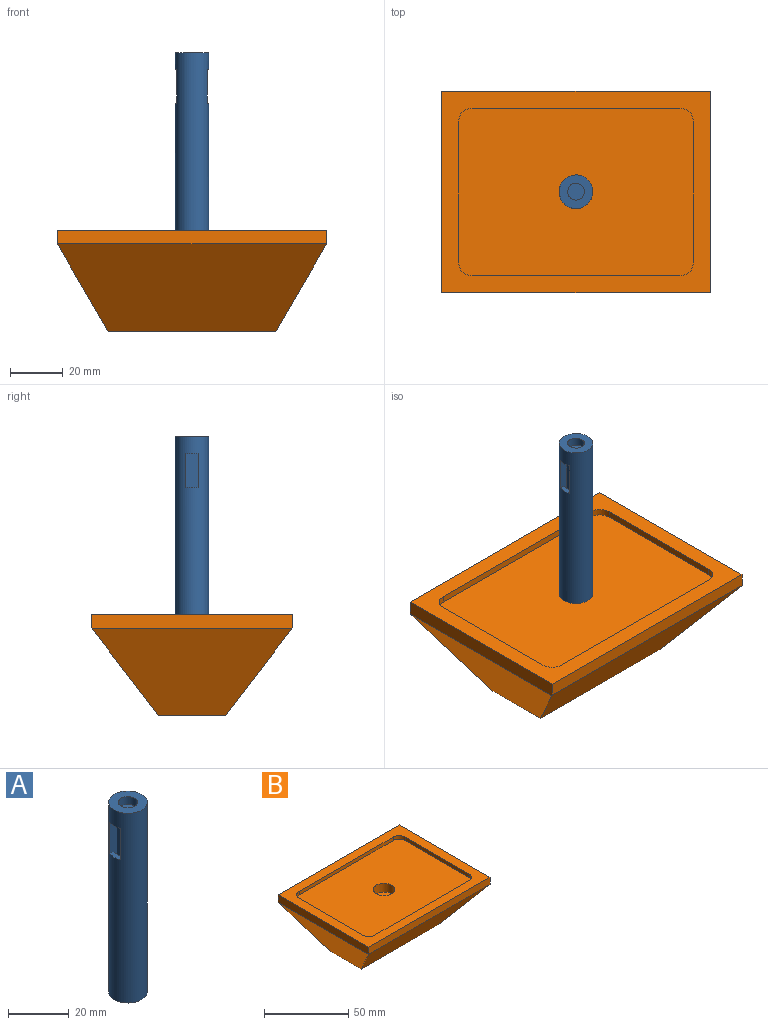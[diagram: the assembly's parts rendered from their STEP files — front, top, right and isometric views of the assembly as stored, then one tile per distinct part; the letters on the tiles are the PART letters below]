
ASSEMBLY  parts=2 mates=1
PART A: 19 faces, bbox 12.7x12.7x76.2 mm
  f0: plane 19.05x5.08mm, normal (1,0,0), area 96.8mm2, adj f1,f2,f3,f6
  f1: plane 31.75x3.28mm, normal (0,1,0), area 77.9mm2, adj f0,f2,f4,f5,f6,f7
  f2: plane 5.08x1.91mm, normal (0,0,1), area 9.7mm2, adj f0,f1,f3,f5
  f3: plane 31.75x3.28mm, normal (0,-1,0), area 77.9mm2, adj f0,f2,f4,f5,f6,f7
  f4: plane 5.08x3.81mm, normal (0,0,-1), area 18.5mm2, adj f1,f3,f5,f7
  f5: plane 31.75x5.08mm, normal (-1,0,0), area 161.3mm2, adj f1,f2,f3,f4
  f6: plane 5.08x1.91mm, normal (0,0,1), area 8.8mm2, adj f0,f1,f3,f7
  f7: cylinder r=6.35mm len=76.2mm, axis (0,0,-1), area 2907.5mm2, adj f1,f3,f4,f6,f9,f10,f12,f14
  f8: plane 19.05x5.08mm, normal (-1,0,0), area 96.8mm2, adj f10,f11,f12,f14
  f9: plane 5.08x3.81mm, normal (0,0,-1), area 18.5mm2, adj f7,f10,f12,f13
  f10: plane 31.75x3.28mm, normal (0,1,0), area 77.9mm2, adj f7,f8,f9,f11,f13,f14
  f11: plane 5.08x1.91mm, normal (0,0,1), area 9.7mm2, adj f8,f10,f12,f13
  f12: plane 31.75x3.28mm, normal (0,-1,0), area 77.9mm2, adj f7,f8,f9,f11,f13,f14
  f13: plane 31.75x5.08mm, normal (1,0,0), area 161.3mm2, adj f9,f10,f11,f12
  f14: plane 5.08x1.91mm, normal (0,0,1), area 8.8mm2, adj f7,f8,f10,f12
  f15: plane 12.7x12.7mm, normal (0,0,1), area 95mm2, adj f7,f17
  f16: plane 12.7x12.7mm, normal (0,0,-1), area 126.7mm2, adj f7
  f17: cylinder r=3.17mm len=6.35mm, axis (0,0,1), area 63.3mm2, adj f15,f18
  f18: plane 6.35x6.35mm, normal (0,0,1), area 31.7mm2, adj f17
PART B: 21 faces, bbox 101.6x76.2x38.1 mm
  f0: plane 101.6x33.02mm, normal (0,-0.79,-0.61), area 3447.7mm2, adj f2,f5,f6,f7,f8,f9
  f1: plane 101.6x33.02mm, normal (0,0.79,-0.61), area 3447.7mm2, adj f2,f3,f6,f7,f8,f9
  f2: plane 76.2x5.44mm, normal (1,0,0), area 414.6mm2, adj f0,f1,f3,f4,f5,f9
  f3: plane 101.6x5.08mm, normal (0,1,0), area 516.1mm2, adj f1,f2,f4,f7
  f4: plane 101.6x76.2mm, normal (0,0,1), area 2118.9mm2, adj f2,f3,f5,f7,f10,f11,f12,f13
  f5: plane 101.6x5.08mm, normal (0,-1,0), area 516.1mm2, adj f0,f2,f4,f7
  f6: plane 63.5x25.4mm, normal (0,0,-1), area 1612.9mm2, adj f0,f1,f8,f9
  f7: plane 76.2x5.44mm, normal (-1,0,0), area 414.6mm2, adj f0,f1,f3,f4,f5,f8
  f8: plane 75.64x32.66mm, normal (-0.86,0,-0.5), area 1910.1mm2, adj f0,f1,f6,f7
  f9: plane 75.64x32.66mm, normal (0.86,0,-0.5), area 1910.1mm2, adj f0,f1,f2,f6
  f10: plane 53.34x2.54mm, normal (-1,0,0), area 135.5mm2, adj f4,f11,f17,f18
  f11: cylinder r=5.08mm len=5.08mm, axis (0,0,1), area 20.3mm2, adj f4,f10,f12,f18
  f12: plane 78.74x2.54mm, normal (0,-1,0), area 200mm2, adj f4,f11,f13,f18
  f13: cylinder r=5.08mm len=5.08mm, axis (0,0,1), area 20.3mm2, adj f4,f12,f14,f18
  f14: plane 53.34x2.54mm, normal (1,0,0), area 135.5mm2, adj f4,f13,f15,f18
  f15: cylinder r=5.08mm len=5.08mm, axis (0,0,1), area 20.3mm2, adj f4,f14,f16,f18
  f16: plane 78.74x2.54mm, normal (0,1,0), area 200mm2, adj f4,f15,f17,f18
  f17: cylinder r=5.08mm len=5.08mm, axis (0,0,1), area 20.3mm2, adj f4,f10,f16,f18
  f18: plane 88.9x63.5mm, normal (0,0,1), area 5496.3mm2, adj f10,f11,f12,f13,f14,f15,f16,f17
  f19: cylinder r=6.35mm len=12.7mm, axis (0,0,1), area 253.4mm2, adj f18,f20
  f20: plane 12.7x12.7mm, normal (0,0,1), area 126.7mm2, adj f19
PLACE A t=(-8.28,6.79,56.16)mm
PLACE B t=(-8.28,6.79,26.95)mm
MATE pin_slot B.f19 <-> A.f7  axis (0,0,1) through (-8.28,6.79,56.16)mm
